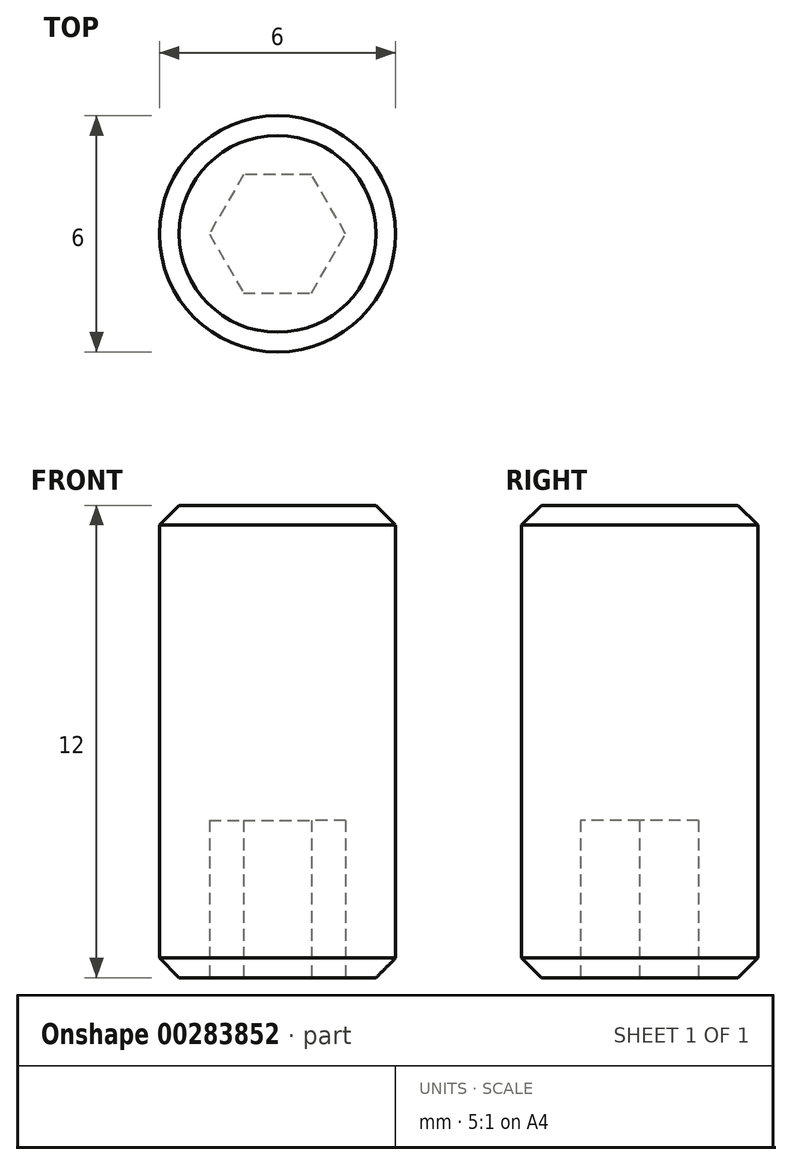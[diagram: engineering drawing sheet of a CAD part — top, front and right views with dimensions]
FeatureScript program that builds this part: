
annotation { "Feature Type Name" : "Feature", "Feature Type Description" : "" }
export const myFeature = defineFeature(function(context is Context, id is Id, definition is map)
    precondition{}
    {
        {
            var Q0;
            Q0=qCreatedBy(makeId("Top.planeOp"),FACE);
            var sketch = newSketch(context, id + "F0", { "sketchPlane" : qUnion([Q0])});
            skCircle(sketch, "E0", {"center": v(0, 0) * mm, "radius": 3 * mm});
            skSolve(sketch);
        }
        {
            var Q0;
            Q0 = qSketchRegion(id + "F0", true);
            extrude(context, id + "F1", {"entities" : qUnion([Q0]), "endBound" : BoundingType.SYMMETRIC, "depth" : 12 * mm});
        }
        {
            var Q0;
            Q0=makeQuery(id+"F1.opExtrude","CAP_EDGE",EDGE,{"disambiguationData":[OSD([sQuery(id+"F0.wireOp",EDGE,"E0")])],"isStart":false});
            var Q1;
            Q1=makeQuery(id+"F1.opExtrude","CAP_EDGE",EDGE,{"disambiguationData":[OSD([sQuery(id+"F0.wireOp",EDGE,"E0")])],"isStart":true});
            chamfer(context, id + "F2", {"entities" : qUnion([Q0, Q1]), "width" : .5 * mm, "tangentPropagation" : true});
        }
        {
            var Q0;
            Q0=makeQuery(id+"F1.opExtrude","CAP_FACE",FACE,{"disambiguationData":[OSD([sQuery(id+"F0.wireOp",EDGE,"E0")])],"isStart":true});
            var sketch = newSketch(context, id + "F3", { "sketchPlane" : qUnion([Q0])});
            skCircle(sketch, "E1.cCircle", {"center": v(0, 0) * mm, "radius": 1.5 * mm, "construction": true});
            skLineSegment(sketch, "E1.0", {"start": v(-0.87, 1.5) * mm, "end": v(0.87, 1.5) * mm});
            skLineSegment(sketch, "E1.1", {"start": v(0.87, 1.5) * mm, "end": v(1.73, 0) * mm});
            skLineSegment(sketch, "E1.2", {"start": v(1.73, 0) * mm, "end": v(0.87, -1.5) * mm});
            skLineSegment(sketch, "E1.3", {"start": v(0.87, -1.5) * mm, "end": v(-0.87, -1.5) * mm});
            skLineSegment(sketch, "E1.4", {"start": v(-0.87, -1.5) * mm, "end": v(-1.73, 0) * mm});
            skLineSegment(sketch, "E1.5", {"start": v(-1.73, 0) * mm, "end": v(-0.87, 1.5) * mm});
            skPoint(sketch, "E1.0.midPoint", {"position": v(0, 1.5) * mm});
            skSolve(sketch);
        }
        {
            var Q0;
            Q0 = qSketchRegion(id + "F3", true);
            extrude(context, id + "F4", {"entities" : qUnion([Q0]), "operationType" : NewBodyOperationType.REMOVE, "oppositeDirection" : true, "depth" : 4 * mm});
        }
    });
